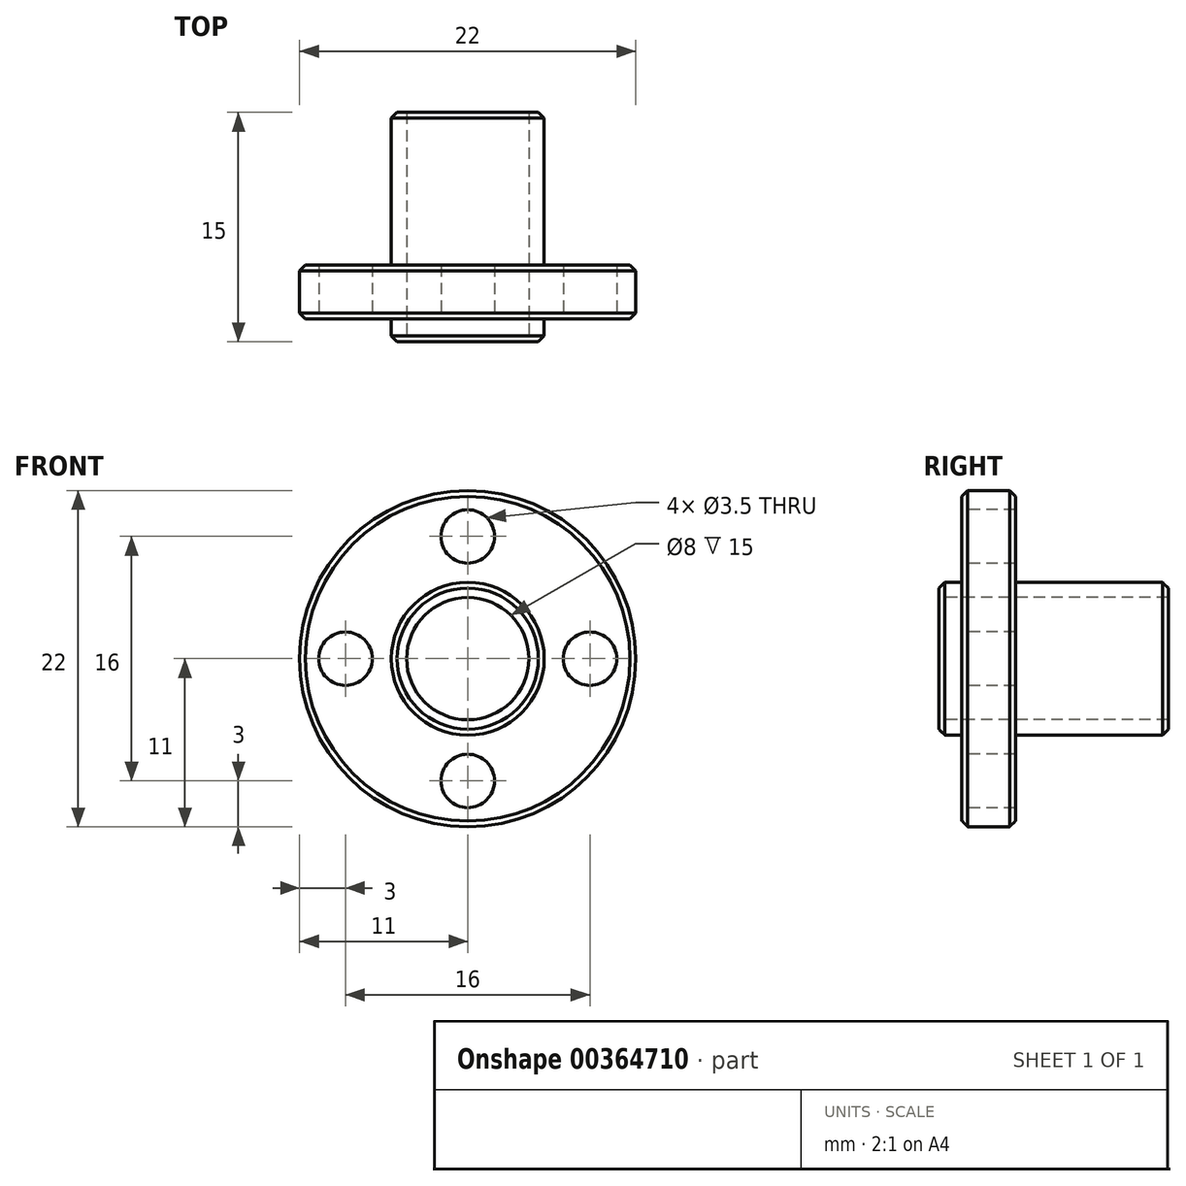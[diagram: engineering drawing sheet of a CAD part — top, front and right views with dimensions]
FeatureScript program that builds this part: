
annotation { "Feature Type Name" : "Feature", "Feature Type Description" : "" }
export const myFeature = defineFeature(function(context is Context, id is Id, definition is map)
    precondition{}
    {
        {
            var Q0;
            Q0=qCreatedBy(makeId("Front.planeOp"),FACE);
            var sketch = newSketch(context, id + "F0", { "sketchPlane" : qUnion([Q0])});
            skCircle(sketch, "E0", {"center": v(0, 0) * mm, "radius": 11 * mm});
            skSolve(sketch);
        }
        {
            var Q0;
            Q0 = qSketchRegion(id + "F0", true);
            extrude(context, id + "F1", {"entities" : qUnion([Q0]), "depth" : 3.5 * mm});
        }
        {
            var Q0;
            Q0=makeQuery(id+"F1.opExtrude","CAP_FACE",FACE,{"disambiguationData":[OSD([sQuery(id+"F0.wireOp",EDGE,"E0")])],"isStart":false});
            var sketch = newSketch(context, id + "F2", { "sketchPlane" : qUnion([Q0])});
            skCircle(sketch, "E1", {"center": v(0, 0) * mm, "radius": 5 * mm});
            skSolve(sketch);
        }
        {
            var Q0;
            Q0 = qSketchRegion(id + "F2", true);
            extrude(context, id + "F3", {"entities" : qUnion([Q0]), "operationType" : NewBodyOperationType.ADD, "depth" : 1.5 * mm});
        }
        {
            var Q0;
            Q0=makeQuery(id+"F1.opExtrude","CAP_FACE",FACE,{"disambiguationData":[OSD([sQuery(id+"F0.wireOp",EDGE,"E0")])],"isStart":true});
            var sketch = newSketch(context, id + "F4", { "sketchPlane" : qUnion([Q0])});
            skCircle(sketch, "E2", {"center": v(0, 0) * mm, "radius": 5 * mm});
            skSolve(sketch);
        }
        {
            var Q0;
            Q0 = qSketchRegion(id + "F4", true);
            extrude(context, id + "F5", {"entities" : qUnion([Q0]), "operationType" : NewBodyOperationType.ADD, "depth" : 10 * mm});
        }
        {
            var Q0;
            Q0=makeQuery(id+"F3.opExtrude","CAP_FACE",FACE,{"disambiguationData":[OSD([sQuery(id+"F2.wireOp",EDGE,"E1")])],"isStart":false});
            var sketch = newSketch(context, id + "F6", { "sketchPlane" : qUnion([Q0])});
            skCircle(sketch, "E3", {"center": v(0, 0) * mm, "radius": 4 * mm});
            skSolve(sketch);
        }
        {
            var Q0;
            Q0 = qSketchRegion(id + "F6", true);
            extrude(context, id + "F7", {"entities" : qUnion([Q0]), "operationType" : NewBodyOperationType.REMOVE, "oppositeDirection" : true, "depth" : 25.4 * mm});
        }
        {
            var Q0;
            Q0=makeQuery(id+"F1.opExtrude","CAP_FACE",FACE,{"disambiguationData":[OSD([sQuery(id+"F0.wireOp",EDGE,"E0")])],"isStart":false});
            var sketch = newSketch(context, id + "F8", { "sketchPlane" : qUnion([Q0])});
            skCircle(sketch, "E4", {"center": v(-8, 0) * mm, "radius": 1.75 * mm});
            skCircle(sketch, "E5", {"center": v(8, 0) * mm, "radius": 1.75 * mm});
            skCircle(sketch, "E6", {"center": v(0, 8) * mm, "radius": 1.75 * mm});
            skCircle(sketch, "E7", {"center": v(0, -8) * mm, "radius": 1.75 * mm});
            skCircle(sketch, "E8", {"center": v(0, 0) * mm, "radius": 8 * mm, "construction": true});
            skSolve(sketch);
        }
        {
            var Q0;
            Q0 = qSketchRegion(id + "F8", true);
            extrude(context, id + "F9", {"entities" : qUnion([Q0]), "operationType" : NewBodyOperationType.REMOVE, "oppositeDirection" : true, "depth" : 25.4 * mm});
        }
        {
            var Q0;
            Q0=makeQuery(id+"F1.opExtrude","SWEPT_FACE",FACE,{"disambiguationData":[OSD([sQuery(id+"F0.wireOp",EDGE,"E0")])]});
            chamfer(context, id + "F10", {"entities" : qUnion([Q0]), "width" : 0.38 * mm, "tangentPropagation" : true});
        }
        {
            var Q0;
            Q0=makeQuery(id+"F5.opExtrude","CAP_EDGE",EDGE,{"disambiguationData":[OSD([sQuery(id+"F4.wireOp",EDGE,"E2")])],"isStart":false});
            var Q1;
            Q1=makeQuery(id+"F3.opExtrude","CAP_EDGE",EDGE,{"disambiguationData":[OSD([sQuery(id+"F2.wireOp",EDGE,"E1")])],"isStart":false});
            chamfer(context, id + "F11", {"entities" : qUnion([Q0, Q1]), "width" : 0.38 * mm, "tangentPropagation" : true});
        }
    });
